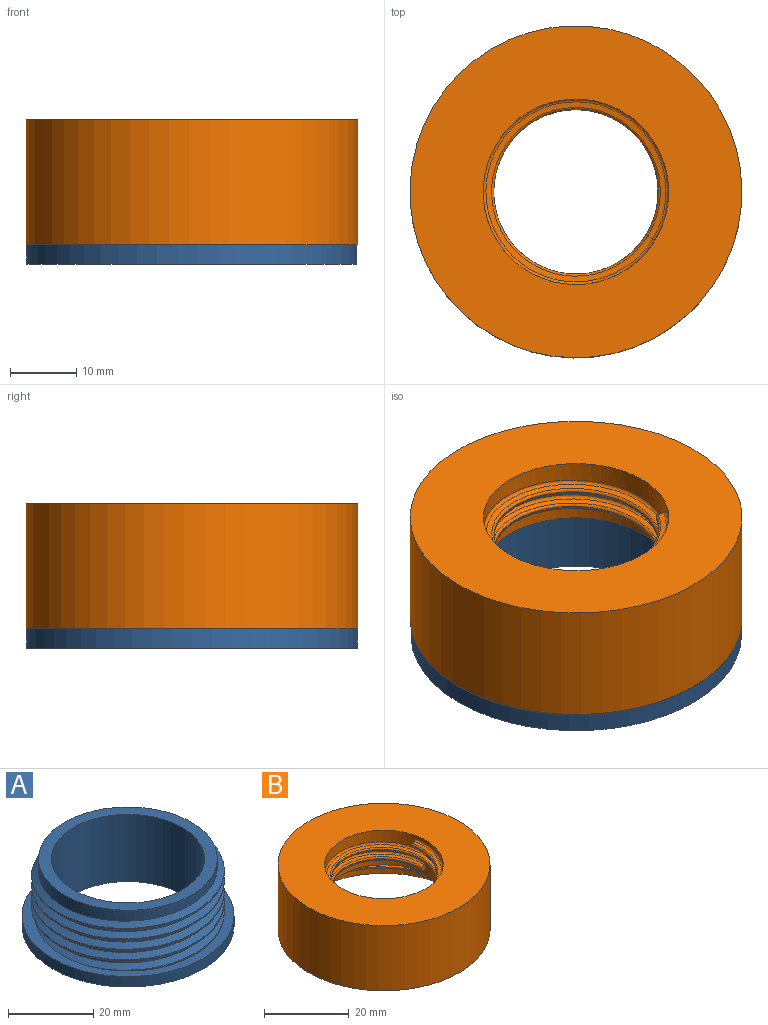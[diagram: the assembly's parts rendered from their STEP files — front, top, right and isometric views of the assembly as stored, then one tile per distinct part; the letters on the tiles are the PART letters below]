
ASSEMBLY  parts=2 mates=1
PART A: 14 faces, bbox 50.7x53.2x20.2 mm
  f0: cylinder r=21mm len=42mm, axis (0,0,-1), area 511.3mm2, adj f1,f9,f10,f11,f13
  f1: cylinder r=21mm len=42mm, axis (0,0,-1), area 99.1mm2, adj f0,f2,f10,f11
  f2: cylinder r=21mm len=42mm, axis (0,0,-1), area 99mm2, adj f1,f3,f10,f11
  f3: cylinder r=21mm len=42mm, axis (0,0,-1), area 99.1mm2, adj f2,f4,f10,f11
  f4: cylinder r=21mm len=42mm, axis (0,0,-1), area 38.9mm2, adj f3,f5,f10,f11
  f5: plane 50.74x50.74mm, normal (0,0,1), area 465.9mm2, adj f4,f6,f10,f11,f12
  f6: cylinder r=24.9mm len=49.8mm, axis (0,0,-1), area 469.4mm2, adj f5,f7
  f7: plane 49.8x49.8mm, normal (0,0,-1), area 929.9mm2, adj f6,f8
  f8: cylinder r=18mm len=36mm, axis (0,0,-1), area 2182.8mm2, adj f7,f9
  f9: plane 42x42mm, normal (0,0,1), area 367.6mm2, adj f0,f8
  f10: bspline ~52.24x45.24mm, area 1181.2mm2, adj f0,f1,f2,f3,f4,f5,f12,f13
  f11: bspline ~52.24x45.24mm, area 1068.3mm2, adj f0,f1,f2,f3,f4,f5,f12,f13
  f12: cylinder r=22.62mm len=45.24mm, axis (0,0,-1), area 241.1mm2, adj f5,f10,f11,f13
  f13: plane 2.25x1.62mm, normal (0,1,0), area 2.1mm2, adj f0,f10,f11,f12
PART B: 26 faces, bbox 51x54.1x19.8 mm
  f0: cylinder r=13.97mm len=27.95mm, axis (0,0,-1), area 231.3mm2, adj f1,f12,f17,f19,f25
  f1: cylinder r=13.97mm len=27.95mm, axis (0,0,-1), area 212.1mm2, adj f0,f2,f18,f19,f25
  f2: plane 50x50mm, normal (0,0,1), area 1350mm2, adj f1,f3
  f3: cylinder r=25mm len=50mm, axis (0,0,-1), area 2953.1mm2, adj f2,f4
  f4: plane 50x50mm, normal (0,0,-1), area 301.6mm2, adj f3,f9
  f5: cylinder r=23mm len=46mm, axis (0,0,-1), area 67.9mm2, adj f6,f10,f15,f16
  f6: cylinder r=23mm len=46mm, axis (0,0,-1), area 108.4mm2, adj f5,f7,f15,f16
  f7: cylinder r=23mm len=46mm, axis (0,0,-1), area 108.4mm2, adj f6,f8,f15,f16
  f8: cylinder r=23mm len=46mm, axis (0,0,-1), area 108.3mm2, adj f7,f9,f15,f16
  f9: cylinder r=23mm len=46mm, axis (0,0,-1), area 426.4mm2, adj f4,f8,f13,f15,f16
  f10: plane 45.71x45.7mm, normal (0,0,-1), area 599.9mm2, adj f5,f11,f14,f15,f16
  f11: cylinder r=17.5mm len=35mm, axis (0,0,-1), area 824.7mm2, adj f10,f12
  f12: plane 35x35mm, normal (0,0,-1), area 348.6mm2, adj f0,f11
  f13: plane 2.25x1.32mm, normal (-0.59,-0.81,0), area 2.1mm2, adj f9,f14,f15,f16
  f14: cylinder r=21.38mm len=42.75mm, axis (0,0,-1), area 242.8mm2, adj f10,f13,f15,f16
  f15: bspline ~53.12x46mm, area 1293.2mm2, adj f5,f6,f7,f8,f9,f10,f13,f14
  f16: bspline ~53.12x46mm, area 1178.1mm2, adj f5,f6,f7,f8,f9,f10,f13,f14
  f17: plane 2.44x1.61mm, normal (0,-1,0), area 2mm2, adj f0,f19,f20,f21,f22,f23,f24,f25
  f18: plane 2.45x1.57mm, normal (-0.23,0.97,0), area 2mm2, adj f1,f19,f20,f21,f22,f23,f24,f25
  f19: bspline ~32.27x27.95mm, area 108.4mm2, adj f0,f1,f17,f18,f20
  f20: bspline ~31.51x27.29mm, area 180.5mm2, adj f17,f18,f19,f21
  f21: bspline ~29.18x25.27mm, area 78.1mm2, adj f17,f18,f20,f22
  f22: cylinder r=12.37mm len=24.75mm, axis (0,0,1), area 28.1mm2, adj f17,f18,f21,f23
  f23: bspline ~29.34x25.41mm, area 89.3mm2, adj f17,f18,f22,f24
  f24: bspline ~31.32x27.12mm, area 146.3mm2, adj f17,f18,f23,f25
  f25: bspline ~32.27x27.95mm, area 123.6mm2, adj f0,f1,f17,f18,f24
PLACE A t=(-4.3,-44.53,-54.76)mm fixed
PLACE B rot(axis=(0,0,-1),45deg) t=(-4.3,-44.53,-6.77)mm
MATE cylindrical A.f0 <-> B.f0  axis (0,0,-1) through (-4.3,-44.53,-48.61)mm
